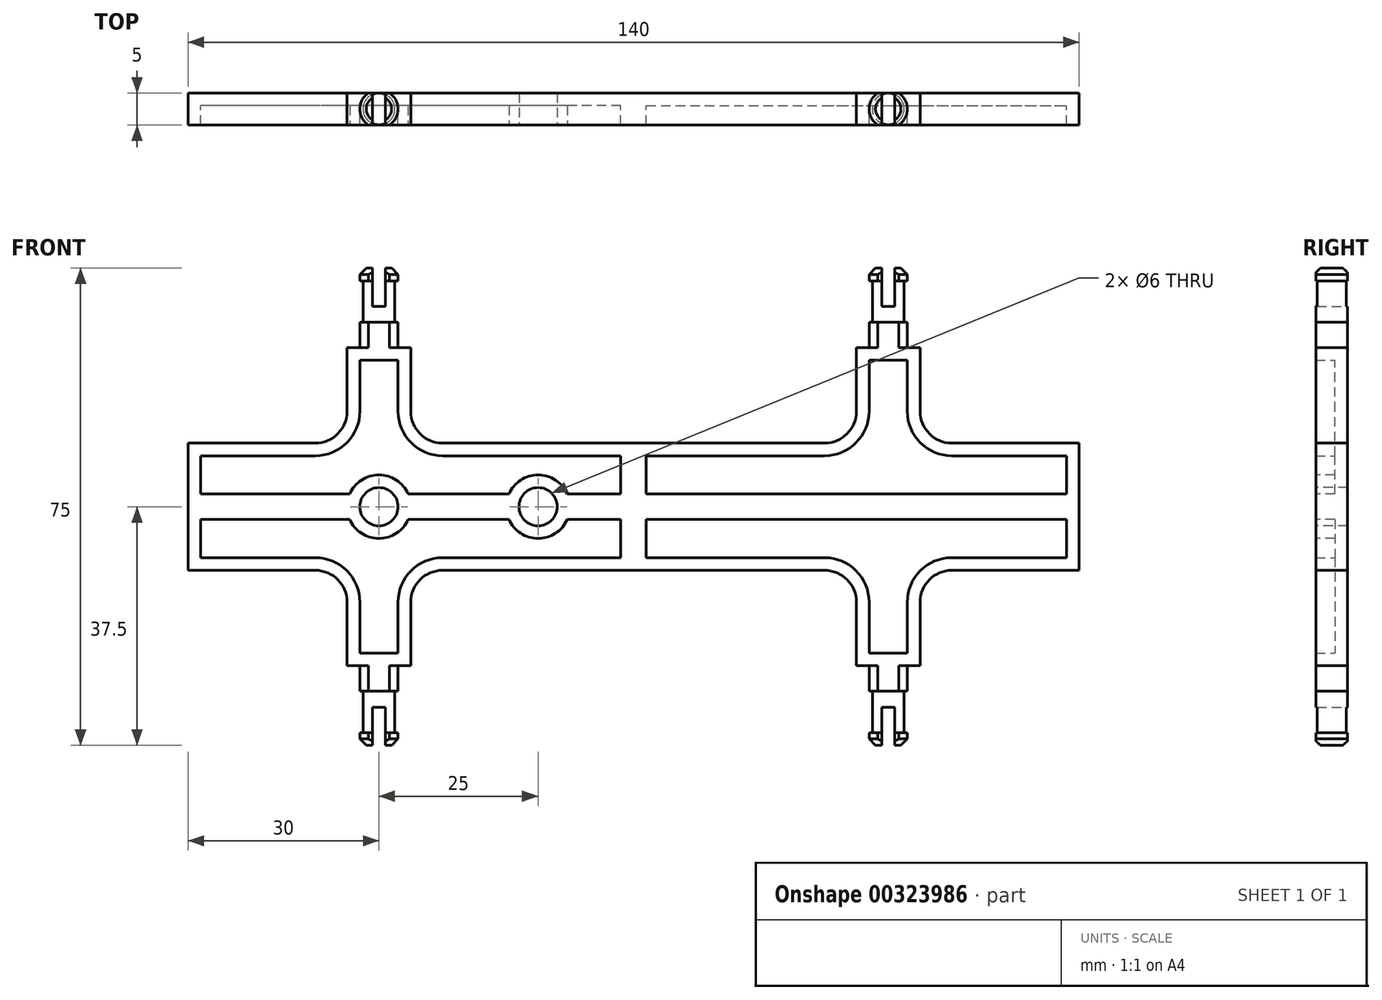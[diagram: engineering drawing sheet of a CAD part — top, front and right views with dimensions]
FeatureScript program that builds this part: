
annotation { "Feature Type Name" : "Feature", "Feature Type Description" : "" }
export const myFeature = defineFeature(function(context is Context, id is Id, definition is map)
    precondition{}
    {
        {
            var Q0;
            Q0=qCreatedBy(makeId("Front.planeOp"),FACE);
            var sketch = newSketch(context, id + "F0", { "sketchPlane" : qUnion([Q0])});
            skLineSegment(sketch, "E0.bottom", {"start": v(0, 0) * mm, "end": v(70, 0) * mm});
            skLineSegment(sketch, "E0.top", {"start": v(0, 10) * mm, "end": v(30, 10) * mm});
            skLineSegment(sketch, "E0.left", {"start": v(0, 0) * mm, "end": v(0, 10) * mm});
            skLineSegment(sketch, "E0.right", {"start": v(70, 0) * mm, "end": v(70, 10) * mm});
            skLineSegment(sketch, "E1.top", {"start": v(35, 25) * mm, "end": v(45, 25) * mm});
            skLineSegment(sketch, "E1.left", {"start": v(35, 15) * mm, "end": v(35, 25) * mm});
            skLineSegment(sketch, "E1.right", {"start": v(45, 15) * mm, "end": v(45, 25) * mm});
            skLineSegment(sketch, "E2.trimOffspring", {"start": v(50, 10) * mm, "end": v(70, 10) * mm});
            skPoint(sketch, "E3.visualSharp", {"position": v(35, 10) * mm});
            skArc(sketch, "E3.filletArc", {"start": v(30, 10) * mm, "mid": v(33.54, 11.46) * mm, "end": v(35, 15) * mm});
            skPoint(sketch, "E4.visualSharp", {"position": v(45, 10) * mm});
            skArc(sketch, "E4.filletArc", {"start": v(45, 15) * mm, "mid": v(46.46, 11.46) * mm, "end": v(50, 10) * mm});
            skSolve(sketch);
        }
        {
            var Q0;
            Q0 = qSketchRegion(id + "F0", true);
            extrude(context, id + "F1", {"entities" : qUnion([Q0]), "endBound" : BoundingType.SYMMETRIC, "depth" : 5 * mm});
        }
        {
            var Q0;
            Q0=makeQuery(id+"F1.opExtrude","CAP_FACE",FACE,{"disambiguationData":[OSD([sQuery(id+"F0.wireOp",EDGE,"E0.bottom"),sQuery(id+"F0.wireOp",EDGE,"E0.top"),sQuery(id+"F0.wireOp",EDGE,"E0.left"),sQuery(id+"F0.wireOp",EDGE,"E0.right"),sQuery(id+"F0.wireOp",EDGE,"E1.top"),sQuery(id+"F0.wireOp",EDGE,"E1.left"),sQuery(id+"F0.wireOp",EDGE,"E1.right"),sQuery(id+"F0.wireOp",EDGE,"E2.trimOffspring"),sQuery(id+"F0.wireOp",EDGE,"E3.filletArc"),sQuery(id+"F0.wireOp",EDGE,"E4.filletArc")])],"isStart":false});
            shell(context, id + "F2", {"entities" : qUnion([Q0]), "thickness" : 2 * mm});
        }
        {
            var Q0;
            Q0=qCreatedBy(makeId("Front.planeOp"),FACE);
            var sketch = newSketch(context, id + "F3", { "sketchPlane" : qUnion([Q0])});
            skLineSegment(sketch, "E5", {"start": v(40, 25) * mm, "end": v(40, 37.5) * mm});
            skLineSegment(sketch, "E6", {"start": v(40, 37.5) * mm, "end": v(37, 37.5) * mm});
            skLineSegment(sketch, "E7", {"start": v(37, 37.5) * mm, "end": v(37, 35.5) * mm});
            skLineSegment(sketch, "E8", {"start": v(37, 35.5) * mm, "end": v(37.5, 35.5) * mm});
            skLineSegment(sketch, "E9", {"start": v(37.5, 35.5) * mm, "end": v(37.5, 29) * mm});
            skLineSegment(sketch, "E10", {"start": v(37.5, 29) * mm, "end": v(37, 29) * mm});
            skLineSegment(sketch, "E11", {"start": v(37, 29) * mm, "end": v(37, 25) * mm});
            skLineSegment(sketch, "E12", {"start": v(37, 25) * mm, "end": v(40, 25) * mm});
            skSolve(sketch);
        }
        {
            var Q0;
            Q0 = qSketchRegion(id + "F3", true);
            var Q1;
            Q1=sQuery(id+"F3.wireOp",EDGE,"E5");
            revolve(context, id + "F4", {"operationType" : NewBodyOperationType.ADD, "entities" : qUnion([Q0]), "axis" : qUnion([Q1]), "revolveType" : RevolveType.FULL});
        }
        {
            var Q0;
            Q0=makeQuery(id+"F4.opRevolve","SWEPT_EDGE",EDGE,{"disambiguationData":[OSD([sQuery(id+"F3.wireOp",EDGE,"E6"),sQuery(id+"F3.wireOp",EDGE,"E7")])]});
            chamfer(context, id + "F5", {"entities" : qUnion([Q0]), "width" : 1 * mm, "tangentPropagation" : true});
        }
        {
            var Q0;
            Q0=makeQuery(id+"F4.opRevolve","SWEPT_FACE",FACE,{"disambiguationData":[OSD([sQuery(id+"F3.wireOp",EDGE,"E6")])]});
            var sketch = newSketch(context, id + "F6", { "sketchPlane" : qUnion([Q0])});
            skLineSegment(sketch, "E13.bottom", {"start": v(-10.91, -2.5) * mm, "end": v(73.94, -2.5) * mm});
            skLineSegment(sketch, "E13.top", {"start": v(-10.91, 2.5) * mm, "end": v(73.94, 2.5) * mm});
            skLineSegment(sketch, "E13.left", {"start": v(-10.91, -2.5) * mm, "end": v(-10.91, 2.5) * mm});
            skLineSegment(sketch, "E13.right", {"start": v(73.94, -2.5) * mm, "end": v(73.94, 2.5) * mm});
            skSolve(sketch);
        }
        {
            var Q0;
            Q0 = qSketchRegion(id + "F6", true);
            extrude(context, id + "F7", {"entities" : qUnion([Q0]), "operationType" : NewBodyOperationType.INTERSECT, "endBound" : BoundingType.THROUGH_ALL, "oppositeDirection" : true, "depth" : 25 * mm});
        }
        {
            var Q0;
            Q0=makeQuery(id+"F4.opRevolve","SWEPT_FACE",FACE,{"disambiguationData":[OSD([sQuery(id+"F3.wireOp",EDGE,"E6")])]});
            var sketch = newSketch(context, id + "F8", { "sketchPlane" : qUnion([Q0])});
            skLineSegment(sketch, "E14.bottom", {"start": v(39, -3.53) * mm, "end": v(41, -3.53) * mm});
            skLineSegment(sketch, "E14.top", {"start": v(39, 3.88) * mm, "end": v(41, 3.88) * mm});
            skLineSegment(sketch, "E14.left", {"start": v(39, -3.53) * mm, "end": v(39, 3.88) * mm});
            skLineSegment(sketch, "E14.right", {"start": v(41, -3.53) * mm, "end": v(41, 3.88) * mm});
            skSolve(sketch);
        }
        {
            var Q0;
            Q0 = qSketchRegion(id + "F8", true);
            extrude(context, id + "F9", {"entities" : qUnion([Q0]), "operationType" : NewBodyOperationType.REMOVE, "oppositeDirection" : true, "depth" : 6 * mm});
        }
        {
            var Q0;
            Q0=makeQuery(id+"F1.opExtrude","SWEPT_BODY",BODY,{"disambiguationData":[OSD([sQuery(id+"F0.wireOp",EDGE,"E0.bottom"),sQuery(id+"F0.wireOp",EDGE,"E0.top"),sQuery(id+"F0.wireOp",EDGE,"E0.left"),sQuery(id+"F0.wireOp",EDGE,"E0.right"),sQuery(id+"F0.wireOp",EDGE,"E1.top"),sQuery(id+"F0.wireOp",EDGE,"E1.left"),sQuery(id+"F0.wireOp",EDGE,"E1.right"),sQuery(id+"F0.wireOp",EDGE,"E2.trimOffspring"),sQuery(id+"F0.wireOp",EDGE,"E3.filletArc"),sQuery(id+"F0.wireOp",EDGE,"E4.filletArc")])]});
            var Q1;
            Q1=qCreatedBy(makeId("Top.planeOp"),FACE);
            mirror(context, id + "F10", {"operationType" : NewBodyOperationType.ADD, "entities" : qUnion([Q0]), "mirrorPlane" : qUnion([Q1])});
        }
        {
            var Q0;
            Q0=makeQuery(id+"F1.opExtrude","SWEPT_BODY",BODY,{"disambiguationData":[OSD([sQuery(id+"F0.wireOp",EDGE,"E0.bottom"),sQuery(id+"F0.wireOp",EDGE,"E0.top"),sQuery(id+"F0.wireOp",EDGE,"E0.left"),sQuery(id+"F0.wireOp",EDGE,"E0.right"),sQuery(id+"F0.wireOp",EDGE,"E1.top"),sQuery(id+"F0.wireOp",EDGE,"E1.left"),sQuery(id+"F0.wireOp",EDGE,"E1.right"),sQuery(id+"F0.wireOp",EDGE,"E2.trimOffspring"),sQuery(id+"F0.wireOp",EDGE,"E3.filletArc"),sQuery(id+"F0.wireOp",EDGE,"E4.filletArc")])]});
            var Q1;
            Q1=qCreatedBy(makeId("Right.planeOp"),FACE);
            mirror(context, id + "F11", {"operationType" : NewBodyOperationType.ADD, "entities" : qUnion([Q0]), "mirrorPlane" : qUnion([Q1])});
        }
        {
            var Q0;
            {var subQ0=makeQuery(id+"F7.boolean.opBoolean","MERGE",FACE,{"derivedFrom":[makeQuery(id+"F1.opExtrude","CAP_FACE",FACE,{"disambiguationData":[OSD([sQuery(id+"F0.wireOp",EDGE,"E0.bottom"),sQuery(id+"F0.wireOp",EDGE,"E0.top"),sQuery(id+"F0.wireOp",EDGE,"E0.left"),sQuery(id+"F0.wireOp",EDGE,"E0.right"),sQuery(id+"F0.wireOp",EDGE,"E1.top"),sQuery(id+"F0.wireOp",EDGE,"E1.left"),sQuery(id+"F0.wireOp",EDGE,"E1.right"),sQuery(id+"F0.wireOp",EDGE,"E2.trimOffspring"),sQuery(id+"F0.wireOp",EDGE,"E3.filletArc"),sQuery(id+"F0.wireOp",EDGE,"E4.filletArc")])],"isStart":false}),makeQuery(id+"F7.boolean.toolComplement.opBoolean","COPY",FACE,{"derivedFrom":makeQuery(id+"F7.opExtrude","SWEPT_FACE",FACE,{"disambiguationData":[OSD([sQuery(id+"F6.wireOp",EDGE,"E13.bottom")])]})})]});var subQ1=makeQuery(id+"F10.boolean.opBoolean","MERGE",FACE,{"derivedFrom":[subQ0,makeQuery(id+"F10.opPattern","COPY",FACE,{"derivedFrom":subQ0,"instanceName":"1"})]});Q0=makeQuery(id+"F11.boolean.opBoolean","MERGE",FACE,{"derivedFrom":[subQ1,makeQuery(id+"F11.opPattern","COPY",FACE,{"derivedFrom":subQ1,"instanceName":"1"})]});}
            var sketch = newSketch(context, id + "F12", { "sketchPlane" : qUnion([Q0])});
            skCircle(sketch, "E15", {"center": v(-40, 0) * mm, "radius": 5 * mm});
            skCircle(sketch, "E16", {"center": v(-15, 0) * mm, "radius": 5 * mm});
            skSolve(sketch);
        }
        {
            var Q0;
            Q0 = qSketchRegion(id + "F12", true);
            extrude(context, id + "F13", {"entities" : qUnion([Q0]), "operationType" : NewBodyOperationType.ADD, "endBound" : BoundingType.UP_TO_NEXT, "oppositeDirection" : true, "depth" : 25 * mm});
        }
        {
            var Q0;
            {var subQ0=makeQuery(id+"F7.boolean.opBoolean","MERGE",FACE,{"derivedFrom":[makeQuery(id+"F1.opExtrude","CAP_FACE",FACE,{"disambiguationData":[OSD([sQuery(id+"F0.wireOp",EDGE,"E0.bottom"),sQuery(id+"F0.wireOp",EDGE,"E0.top"),sQuery(id+"F0.wireOp",EDGE,"E0.left"),sQuery(id+"F0.wireOp",EDGE,"E0.right"),sQuery(id+"F0.wireOp",EDGE,"E1.top"),sQuery(id+"F0.wireOp",EDGE,"E1.left"),sQuery(id+"F0.wireOp",EDGE,"E1.right"),sQuery(id+"F0.wireOp",EDGE,"E2.trimOffspring"),sQuery(id+"F0.wireOp",EDGE,"E3.filletArc"),sQuery(id+"F0.wireOp",EDGE,"E4.filletArc")])],"isStart":false}),makeQuery(id+"F7.boolean.toolComplement.opBoolean","COPY",FACE,{"derivedFrom":makeQuery(id+"F7.opExtrude","SWEPT_FACE",FACE,{"disambiguationData":[OSD([sQuery(id+"F6.wireOp",EDGE,"E13.bottom")])]})})]});var subQ1=makeQuery(id+"F10.boolean.opBoolean","MERGE",FACE,{"derivedFrom":[subQ0,makeQuery(id+"F10.opPattern","COPY",FACE,{"derivedFrom":subQ0,"instanceName":"1"})]});Q0=makeQuery(id+"F13.boolean.opBoolean","MERGE",FACE,{"derivedFrom":[makeQuery(id+"F11.boolean.opBoolean","MERGE",FACE,{"derivedFrom":[subQ1,makeQuery(id+"F11.opPattern","COPY",FACE,{"derivedFrom":subQ1,"instanceName":"1"})]}),makeQuery(id+"F13.opExtrude","CAP_FACE",FACE,{"disambiguationData":[OSD([sQuery(id+"F12.wireOp",EDGE,"E15")])],"isStart":true}),makeQuery(id+"F13.opExtrude","CAP_FACE",FACE,{"disambiguationData":[OSD([sQuery(id+"F12.wireOp",EDGE,"E16")])],"isStart":true})]});}
            var sketch = newSketch(context, id + "F14", { "sketchPlane" : qUnion([Q0])});
            skPoint(sketch, "E17", {"position": v(-40, 0) * mm});
            skPoint(sketch, "E18", {"position": v(-15, 0) * mm});
            skSolve(sketch);
        }
        {
            var Q0;
            Q0=sQuery(id+"F14.wireOp",VERTEX,"E17");
            var Q1;
            Q1=sQuery(id+"F14.wireOp",VERTEX,"E18");
            var Q2;
            Q2=makeQuery(id+"F1.opExtrude","SWEPT_BODY",BODY,{"disambiguationData":[OSD([sQuery(id+"F0.wireOp",EDGE,"E0.bottom"),sQuery(id+"F0.wireOp",EDGE,"E0.top"),sQuery(id+"F0.wireOp",EDGE,"E0.left"),sQuery(id+"F0.wireOp",EDGE,"E0.right"),sQuery(id+"F0.wireOp",EDGE,"E1.top"),sQuery(id+"F0.wireOp",EDGE,"E1.left"),sQuery(id+"F0.wireOp",EDGE,"E1.right"),sQuery(id+"F0.wireOp",EDGE,"E2.trimOffspring"),sQuery(id+"F0.wireOp",EDGE,"E3.filletArc"),sQuery(id+"F0.wireOp",EDGE,"E4.filletArc")])]});
            hole(context, id + "F15", {"style" : HoleStyle.SIMPLE, "endStyle" : HoleEndStyle.THROUGH, "holeDiameter" : 6 * mm, "isTappedThrough" : true, "tappedDepth" : 12 * mm, "tapClearance" : 3, "locations" : qUnion([Q0, Q1]), "scope" : qUnion([Q2])});
        }
    });
